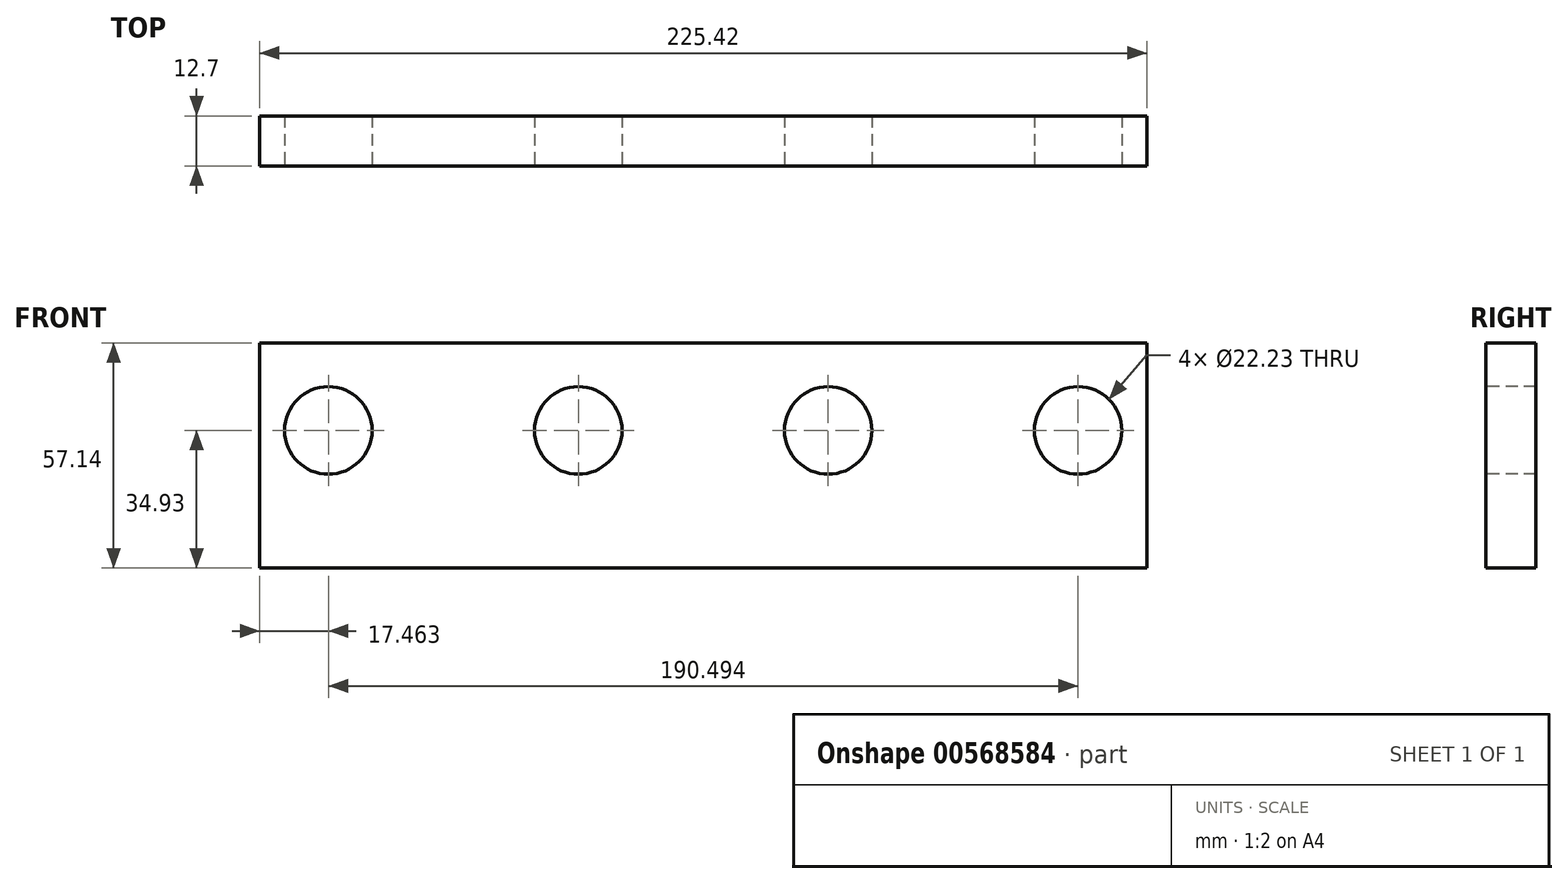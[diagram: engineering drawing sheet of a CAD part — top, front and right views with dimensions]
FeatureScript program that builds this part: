
annotation { "Feature Type Name" : "Feature", "Feature Type Description" : "" }
export const myFeature = defineFeature(function(context is Context, id is Id, definition is map)
    precondition{}
    {
        {
            var Q0;
            Q0=qCreatedBy(makeId("Front.planeOp"),FACE);
            var sketch = newSketch(context, id + "F0", { "sketchPlane" : qUnion([Q0])});
            skLineSegment(sketch, "E0.bottom", {"start": v(-112.71, 28.57) * mm, "end": v(112.71, 28.57) * mm});
            skLineSegment(sketch, "E0.top", {"start": v(-112.71, -28.57) * mm, "end": v(112.71, -28.57) * mm});
            skLineSegment(sketch, "E0.left", {"start": v(-112.71, 28.57) * mm, "end": v(-112.71, -28.57) * mm});
            skLineSegment(sketch, "E0.right", {"start": v(112.71, 28.57) * mm, "end": v(112.71, -28.57) * mm});
            skPoint(sketch, "E0.middle", {"position": v(0, 0) * mm});
            skSolve(sketch);
        }
        {
            var Q0;
            Q0 = qSketchRegion(id + "F0", true);
            extrude(context, id + "F1", {"entities" : qUnion([Q0]), "depth" : 12.7 * mm, "offsetDistance" : 25.4 * mm, "symmetric" : true});
        }
        {
            var Q0;
            Q0=makeQuery(id+"F1.opExtrude","CAP_FACE",FACE,{"disambiguationData":[OSD([sQuery(id+"F0.wireOp",EDGE,"E0.bottom"),sQuery(id+"F0.wireOp",EDGE,"E0.top"),sQuery(id+"F0.wireOp",EDGE,"E0.left"),sQuery(id+"F0.wireOp",EDGE,"E0.right")])],"isStart":false});
            var sketch = newSketch(context, id + "F2", { "sketchPlane" : qUnion([Q0])});
            skLineSegment(sketch, "E1", {"start": v(-109.4, 6.36) * mm, "end": v(-81.1, 6.36) * mm});
            skCircle(sketch, "E2", {"center": v(-95.25, 6.36) * mm, "radius": 11.11 * mm});
            skLineSegment(sketch, "E3", {"start": v(-44.45, 6.36) * mm, "end": v(-19.05, 6.36) * mm});
            skPoint(sketch, "E4", {"position": v(-31.75, 6.36) * mm});
            skCircle(sketch, "E5", {"center": v(-31.75, 6.36) * mm, "radius": 11.11 * mm});
            skLineSegment(sketch, "E6", {"start": v(19.05, 6.36) * mm, "end": v(44.45, 6.36) * mm});
            skPoint(sketch, "E7", {"position": v(31.75, 6.36) * mm});
            skLineSegment(sketch, "E8", {"start": v(82.55, 6.36) * mm, "end": v(107.95, 6.36) * mm});
            skPoint(sketch, "E9", {"position": v(95.25, 6.36) * mm});
            skCircle(sketch, "E10", {"center": v(31.75, 6.36) * mm, "radius": 11.11 * mm});
            skCircle(sketch, "E11", {"center": v(95.25, 6.36) * mm, "radius": 11.11 * mm});
            skSolve(sketch);
        }
        {
            var Q0;
            {var subQ0=sQuery(id+"F2.wireOp",EDGE,"E2");var subQ1=sQuery(id+"F2.wireOp",EDGE,"E1");var subQ2=makeQuery(id+"F2.imprint","INTERSECT",VERTEX,{"disambiguationData":[OD(0.0)],"derivedFrom":[subQ1,subQ0]});Q0=makeQuery(id+"F2.imprint","IMPRINT",FACE,{"disambiguationData":[TD([[makeQuery(id+"F2.imprint","IMPRINT",EDGE,{"disambiguationData":[TD([[subQ2,-1.0]])],"derivedFrom":subQ1}),-1.0]])]});}
            var Q1;
            {var subQ0=sQuery(id+"F2.wireOp",EDGE,"E2");var subQ1=sQuery(id+"F2.wireOp",EDGE,"E1");var subQ2=makeQuery(id+"F2.imprint","INTERSECT",VERTEX,{"disambiguationData":[OD(0.0)],"derivedFrom":[subQ1,subQ0]});Q1=makeQuery(id+"F2.imprint","IMPRINT",FACE,{"disambiguationData":[TD([[makeQuery(id+"F2.imprint","IMPRINT",EDGE,{"disambiguationData":[TD([[subQ2,-1.0]])],"derivedFrom":subQ1}),1.0]])]});}
            var Q2;
            {var subQ0=sQuery(id+"F2.wireOp",EDGE,"E5");var subQ1=sQuery(id+"F2.wireOp",EDGE,"E3");var subQ2=makeQuery(id+"F2.imprint","INTERSECT",VERTEX,{"disambiguationData":[OD(0.0)],"derivedFrom":[subQ1,subQ0]});Q2=makeQuery(id+"F2.imprint","IMPRINT",FACE,{"disambiguationData":[TD([[makeQuery(id+"F2.imprint","IMPRINT",EDGE,{"disambiguationData":[TD([[subQ2,-1.0]])],"derivedFrom":subQ1}),-1.0]])]});}
            var Q3;
            {var subQ0=sQuery(id+"F2.wireOp",EDGE,"E5");var subQ1=sQuery(id+"F2.wireOp",EDGE,"E3");var subQ2=makeQuery(id+"F2.imprint","INTERSECT",VERTEX,{"disambiguationData":[OD(0.0)],"derivedFrom":[subQ1,subQ0]});Q3=makeQuery(id+"F2.imprint","IMPRINT",FACE,{"disambiguationData":[TD([[makeQuery(id+"F2.imprint","IMPRINT",EDGE,{"disambiguationData":[TD([[subQ2,-1.0]])],"derivedFrom":subQ1}),1.0]])]});}
            var Q4;
            {var subQ0=sQuery(id+"F2.wireOp",EDGE,"E10");var subQ1=sQuery(id+"F2.wireOp",EDGE,"E6");var subQ2=makeQuery(id+"F2.imprint","INTERSECT",VERTEX,{"disambiguationData":[OD(0.0)],"derivedFrom":[subQ1,subQ0]});Q4=makeQuery(id+"F2.imprint","IMPRINT",FACE,{"disambiguationData":[TD([[makeQuery(id+"F2.imprint","IMPRINT",EDGE,{"disambiguationData":[TD([[subQ2,-1.0]])],"derivedFrom":subQ1}),-1.0]])]});}
            var Q5;
            {var subQ0=sQuery(id+"F2.wireOp",EDGE,"E10");var subQ1=sQuery(id+"F2.wireOp",EDGE,"E6");var subQ2=makeQuery(id+"F2.imprint","INTERSECT",VERTEX,{"disambiguationData":[OD(0.0)],"derivedFrom":[subQ1,subQ0]});Q5=makeQuery(id+"F2.imprint","IMPRINT",FACE,{"disambiguationData":[TD([[makeQuery(id+"F2.imprint","IMPRINT",EDGE,{"disambiguationData":[TD([[subQ2,-1.0]])],"derivedFrom":subQ1}),1.0]])]});}
            var Q6;
            {var subQ0=sQuery(id+"F2.wireOp",EDGE,"E11");var subQ1=sQuery(id+"F2.wireOp",EDGE,"E8");var subQ2=makeQuery(id+"F2.imprint","INTERSECT",VERTEX,{"disambiguationData":[OD(0.0)],"derivedFrom":[subQ1,subQ0]});Q6=makeQuery(id+"F2.imprint","IMPRINT",FACE,{"disambiguationData":[TD([[makeQuery(id+"F2.imprint","IMPRINT",EDGE,{"disambiguationData":[TD([[subQ2,-1.0]])],"derivedFrom":subQ1}),-1.0]])]});}
            var Q7;
            {var subQ0=sQuery(id+"F2.wireOp",EDGE,"E11");var subQ1=sQuery(id+"F2.wireOp",EDGE,"E8");var subQ2=makeQuery(id+"F2.imprint","INTERSECT",VERTEX,{"disambiguationData":[OD(0.0)],"derivedFrom":[subQ1,subQ0]});Q7=makeQuery(id+"F2.imprint","IMPRINT",FACE,{"disambiguationData":[TD([[makeQuery(id+"F2.imprint","IMPRINT",EDGE,{"disambiguationData":[TD([[subQ2,-1.0]])],"derivedFrom":subQ1}),1.0]])]});}
            extrude(context, id + "F3", {"entities" : qUnion([Q0, Q1, Q2, Q3, Q4, Q5, Q6, Q7]), "operationType" : NewBodyOperationType.REMOVE, "endBound" : BoundingType.THROUGH_ALL, "oppositeDirection" : true, "depth" : 9.52 * mm, "offsetDistance" : 25.4 * mm});
        }
    });
